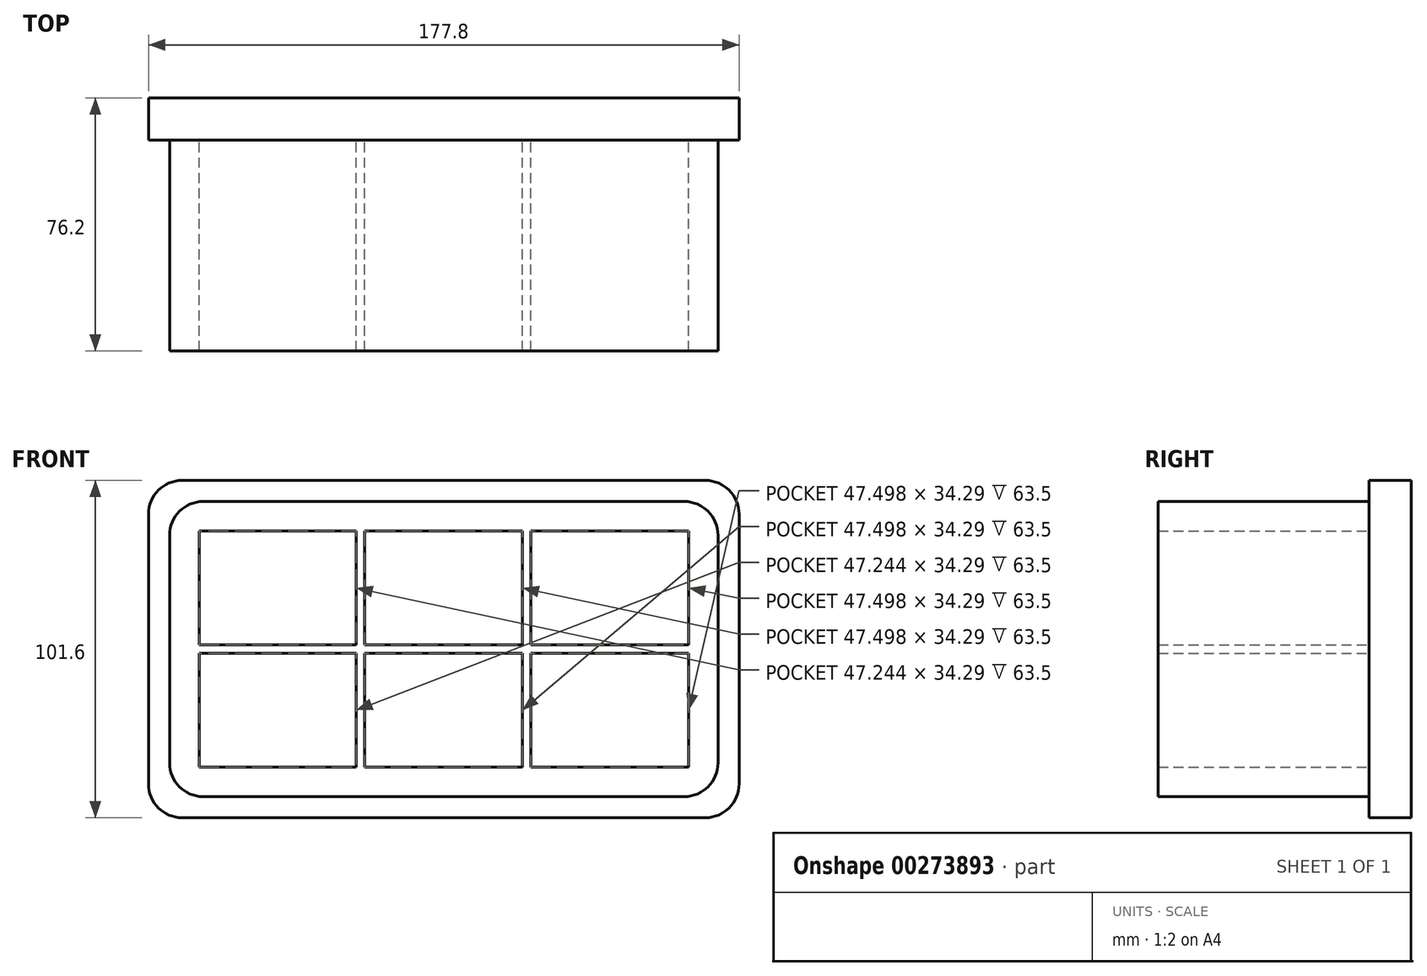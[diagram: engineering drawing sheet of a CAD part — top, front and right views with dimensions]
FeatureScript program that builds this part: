
annotation { "Feature Type Name" : "Feature", "Feature Type Description" : "" }
export const myFeature = defineFeature(function(context is Context, id is Id, definition is map)
    precondition{}
    {
        {
            var Q0;
            Q0=qCreatedBy(makeId("Front.planeOp"),FACE);
            var sketch = newSketch(context, id + "F0", { "sketchPlane" : qUnion([Q0])});
            skLineSegment(sketch, "E0.bottom", {"start": v(76.2, -38.1) * mm, "end": v(-76.2, -38.1) * mm});
            skLineSegment(sketch, "E0.top", {"start": v(76.2, 38.1) * mm, "end": v(-76.2, 38.1) * mm});
            skLineSegment(sketch, "E0.left", {"start": v(76.2, -38.1) * mm, "end": v(76.2, 38.1) * mm});
            skLineSegment(sketch, "E0.right", {"start": v(-76.2, -38.1) * mm, "end": v(-76.2, 38.1) * mm});
            skPoint(sketch, "E0.middle", {"position": v(0, 0) * mm});
            skLineSegment(sketch, "E1.bottom", {"start": v(-73.66, 35.56) * mm, "end": v(-26.42, 35.56) * mm});
            skLineSegment(sketch, "E1.top", {"start": v(-73.66, 1.27) * mm, "end": v(-26.42, 1.27) * mm});
            skLineSegment(sketch, "E1.left", {"start": v(-73.66, 35.56) * mm, "end": v(-73.66, 1.27) * mm});
            skLineSegment(sketch, "E1.right", {"start": v(-26.42, 35.56) * mm, "end": v(-26.42, 1.27) * mm});
            skLineSegment(sketch, "E2.bottom", {"start": v(-23.88, 35.56) * mm, "end": v(23.62, 35.56) * mm});
            skLineSegment(sketch, "E2.top", {"start": v(-23.88, 1.27) * mm, "end": v(23.62, 1.27) * mm});
            skLineSegment(sketch, "E2.left", {"start": v(-23.88, 35.56) * mm, "end": v(-23.88, 1.27) * mm});
            skLineSegment(sketch, "E2.right", {"start": v(23.62, 35.56) * mm, "end": v(23.62, 1.27) * mm});
            skLineSegment(sketch, "E3.bottom", {"start": v(26.16, 35.56) * mm, "end": v(73.66, 35.56) * mm});
            skLineSegment(sketch, "E3.top", {"start": v(26.16, 1.27) * mm, "end": v(73.66, 1.27) * mm});
            skLineSegment(sketch, "E3.left", {"start": v(26.16, 35.56) * mm, "end": v(26.16, 1.27) * mm});
            skLineSegment(sketch, "E3.right", {"start": v(73.66, 35.56) * mm, "end": v(73.66, 1.27) * mm});
            skLineSegment(sketch, "E4.bottom", {"start": v(-73.66, -1.27) * mm, "end": v(-26.42, -1.27) * mm});
            skLineSegment(sketch, "E4.top", {"start": v(-73.66, -35.56) * mm, "end": v(-26.42, -35.56) * mm});
            skLineSegment(sketch, "E4.left", {"start": v(-73.66, -1.27) * mm, "end": v(-73.66, -35.56) * mm});
            skLineSegment(sketch, "E4.right", {"start": v(-26.42, -1.27) * mm, "end": v(-26.42, -35.56) * mm});
            skLineSegment(sketch, "E5.bottom", {"start": v(-23.88, -1.27) * mm, "end": v(23.62, -1.27) * mm});
            skLineSegment(sketch, "E5.top", {"start": v(-23.88, -35.56) * mm, "end": v(23.62, -35.56) * mm});
            skLineSegment(sketch, "E5.left", {"start": v(-23.88, -1.27) * mm, "end": v(-23.88, -35.56) * mm});
            skLineSegment(sketch, "E5.right", {"start": v(23.62, -1.27) * mm, "end": v(23.62, -35.56) * mm});
            skLineSegment(sketch, "E6.bottom", {"start": v(26.16, -1.27) * mm, "end": v(73.66, -1.27) * mm});
            skLineSegment(sketch, "E6.top", {"start": v(26.16, -35.56) * mm, "end": v(73.66, -35.56) * mm});
            skLineSegment(sketch, "E6.left", {"start": v(26.16, -1.27) * mm, "end": v(26.16, -35.56) * mm});
            skLineSegment(sketch, "E6.right", {"start": v(73.66, -1.27) * mm, "end": v(73.66, -35.56) * mm});
            skLineSegment(sketch, "E7.bottom", {"start": v(82.55, -44.45) * mm, "end": v(-82.55, -44.45) * mm});
            skLineSegment(sketch, "E7.top", {"start": v(82.55, 44.45) * mm, "end": v(-82.55, 44.45) * mm});
            skLineSegment(sketch, "E7.left", {"start": v(82.55, -44.45) * mm, "end": v(82.55, 44.45) * mm});
            skLineSegment(sketch, "E7.right", {"start": v(-82.55, -44.45) * mm, "end": v(-82.55, 44.45) * mm});
            skSolve(sketch);
        }
        {
            var Q0;
            Q0=makeQuery(id+"F0.imprint","IMPRINT",FACE,{"disambiguationData":[TD([[makeQuery(id+"F0.imprint","IMPRINT",EDGE,{"derivedFrom":sQuery(id+"F0.wireOp",EDGE,"E0.bottom")}),1.0]])]});
            extrude(context, id + "F1", {"entities" : qUnion([Q0]), "depth" : 76.2 * mm});
        }
        {
            var Q0;
            Q0=makeQuery(id+"F0.imprint","IMPRINT",FACE,{"disambiguationData":[TD([[makeQuery(id+"F0.imprint","IMPRINT",EDGE,{"derivedFrom":sQuery(id+"F0.wireOp",EDGE,"E0.bottom")}),-1.0]])]});
            extrude(context, id + "F2", {"entities" : qUnion([Q0]), "operationType" : NewBodyOperationType.ADD, "depth" : 76.2 * mm});
        }
        {
            var Q0;
            Q0=makeQuery(id+"F1.opExtrude","SWEPT_EDGE",EDGE,{"disambiguationData":[OSD([sQuery(id+"F0.wireOp",EDGE,"E7.bottom"),sQuery(id+"F0.wireOp",EDGE,"E7.right")])]});
            var Q1;
            Q1=makeQuery(id+"F1.opExtrude","SWEPT_EDGE",EDGE,{"disambiguationData":[OSD([sQuery(id+"F0.wireOp",EDGE,"E7.bottom"),sQuery(id+"F0.wireOp",EDGE,"E7.left")])]});
            var Q2;
            Q2=makeQuery(id+"F1.opExtrude","SWEPT_EDGE",EDGE,{"disambiguationData":[OSD([sQuery(id+"F0.wireOp",EDGE,"E7.top"),sQuery(id+"F0.wireOp",EDGE,"E7.right")])]});
            var Q3;
            Q3=makeQuery(id+"F1.opExtrude","SWEPT_EDGE",EDGE,{"disambiguationData":[OSD([sQuery(id+"F0.wireOp",EDGE,"E7.top"),sQuery(id+"F0.wireOp",EDGE,"E7.left")])]});
            fillet(context, id + "F3", {"entities" : qUnion([Q0, Q1, Q2, Q3]), "radius" : 10.16 * mm, "tangentPropagation" : true, "allowEdgeOverflow" : false});
        }
        {
            var Q0;
            Q0=qCreatedBy(makeId("Front.planeOp"),FACE);
            var sketch = newSketch(context, id + "F4", { "sketchPlane" : qUnion([Q0])});
            skLineSegment(sketch, "E8.bottom", {"start": v(88.9, 50.8) * mm, "end": v(-88.9, 50.8) * mm});
            skLineSegment(sketch, "E8.top", {"start": v(88.9, -50.8) * mm, "end": v(-88.9, -50.8) * mm});
            skLineSegment(sketch, "E8.left", {"start": v(88.9, 50.8) * mm, "end": v(88.9, -50.8) * mm});
            skLineSegment(sketch, "E8.right", {"start": v(-88.9, 50.8) * mm, "end": v(-88.9, -50.8) * mm});
            skPoint(sketch, "E8.middle", {"position": v(0, 0) * mm});
            skSolve(sketch);
        }
        {
            var Q0;
            Q0=makeQuery(id+"F4.imprint","IMPRINT",FACE,{"disambiguationData":[TD([[makeQuery(id+"F4.imprint","IMPRINT",EDGE,{"derivedFrom":sQuery(id+"F4.wireOp",EDGE,"E8.bottom")}),1.0]])]});
            extrude(context, id + "F5", {"entities" : qUnion([Q0]), "operationType" : NewBodyOperationType.ADD, "depth" : 12.7 * mm});
        }
        {
            var Q0;
            Q0=makeQuery(id+"F5.opExtrude","SWEPT_EDGE",EDGE,{"disambiguationData":[OSD([sQuery(id+"FpNOHbTcnAcnyxv_1.wireOp",EDGE,"ngFkyO57-Yskc-wnCm-ATkV-n0hatR46mY8b.top"),sQuery(id+"FpNOHbTcnAcnyxv_1.wireOp",EDGE,"ngFkyO57-Yskc-wnCm-ATkV-n0hatR46mY8b.right")])]});
            var Q1;
            Q1=makeQuery(id+"F5.opExtrude","SWEPT_EDGE",EDGE,{"disambiguationData":[OSD([sQuery(id+"FpNOHbTcnAcnyxv_1.wireOp",EDGE,"ngFkyO57-Yskc-wnCm-ATkV-n0hatR46mY8b.top"),sQuery(id+"FpNOHbTcnAcnyxv_1.wireOp",EDGE,"ngFkyO57-Yskc-wnCm-ATkV-n0hatR46mY8b.left")])]});
            var Q2;
            Q2=makeQuery(id+"F5.opExtrude","SWEPT_EDGE",EDGE,{"disambiguationData":[OSD([sQuery(id+"FpNOHbTcnAcnyxv_1.wireOp",EDGE,"ngFkyO57-Yskc-wnCm-ATkV-n0hatR46mY8b.bottom"),sQuery(id+"FpNOHbTcnAcnyxv_1.wireOp",EDGE,"ngFkyO57-Yskc-wnCm-ATkV-n0hatR46mY8b.right")])]});
            var Q3;
            Q3=makeQuery(id+"F5.opExtrude","SWEPT_EDGE",EDGE,{"disambiguationData":[OSD([sQuery(id+"FpNOHbTcnAcnyxv_1.wireOp",EDGE,"ngFkyO57-Yskc-wnCm-ATkV-n0hatR46mY8b.bottom"),sQuery(id+"FpNOHbTcnAcnyxv_1.wireOp",EDGE,"ngFkyO57-Yskc-wnCm-ATkV-n0hatR46mY8b.left")])]});
            var Q4;
            Q4=makeQuery(id+"F5.opExtrude","SWEPT_EDGE",EDGE,{"disambiguationData":[OSD([sQuery(id+"F4.wireOp",EDGE,"E8.bottom"),sQuery(id+"F4.wireOp",EDGE,"E8.right")])]});
            var Q5;
            Q5=makeQuery(id+"F5.opExtrude","SWEPT_EDGE",EDGE,{"disambiguationData":[OSD([sQuery(id+"F4.wireOp",EDGE,"E8.bottom"),sQuery(id+"F4.wireOp",EDGE,"E8.left")])]});
            var Q6;
            Q6=makeQuery(id+"F5.opExtrude","SWEPT_EDGE",EDGE,{"disambiguationData":[OSD([sQuery(id+"F4.wireOp",EDGE,"E8.top"),sQuery(id+"F4.wireOp",EDGE,"E8.right")])]});
            var Q7;
            Q7=makeQuery(id+"F5.opExtrude","SWEPT_EDGE",EDGE,{"disambiguationData":[OSD([sQuery(id+"F4.wireOp",EDGE,"E8.top"),sQuery(id+"F4.wireOp",EDGE,"E8.left")])]});
            fillet(context, id + "F6", {"entities" : qUnion([Q0, Q1, Q2, Q3, Q4, Q5, Q6, Q7]), "radius" : 10.16 * mm, "tangentPropagation" : true, "allowEdgeOverflow" : false});
        }
    });
